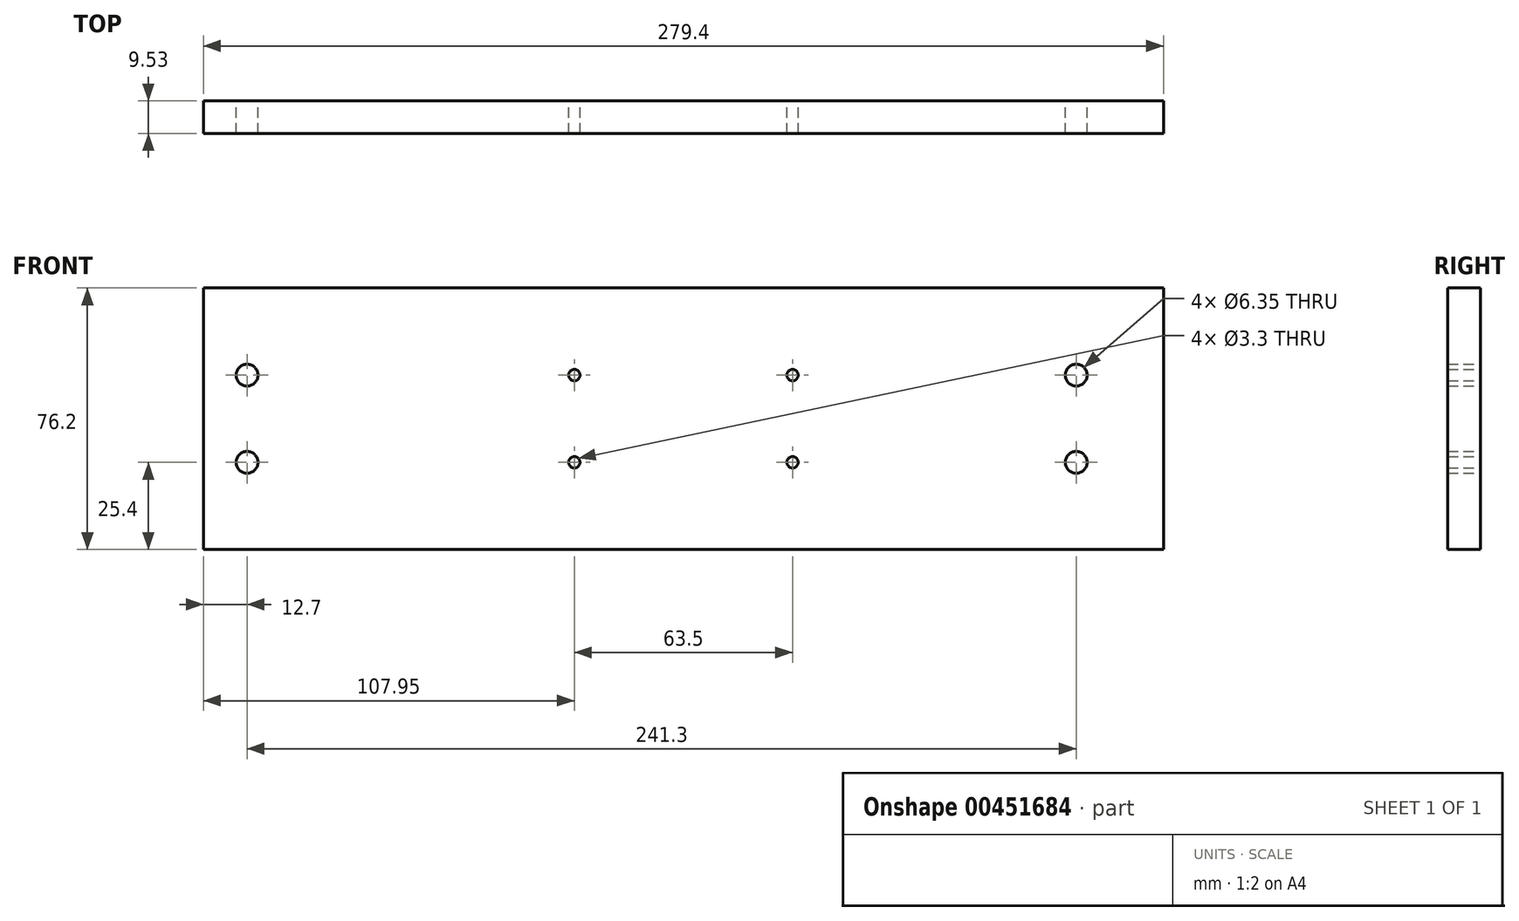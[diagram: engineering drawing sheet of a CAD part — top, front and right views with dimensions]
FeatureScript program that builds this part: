
annotation { "Feature Type Name" : "Feature", "Feature Type Description" : "" }
export const myFeature = defineFeature(function(context is Context, id is Id, definition is map)
    precondition{}
    {
        {
            var Q0;
            Q0=qCreatedBy(makeId("Front.planeOp"),FACE);
            var sketch = newSketch(context, id + "F0", { "sketchPlane" : qUnion([Q0])});
            skLineSegment(sketch, "E0.bottom", {"start": v(-139.7, 38.1) * mm, "end": v(139.7, 38.1) * mm});
            skLineSegment(sketch, "E0.left", {"start": v(-139.7, 38.1) * mm, "end": v(-139.7, 0) * mm});
            skLineSegment(sketch, "E0.right", {"start": v(139.7, 38.1) * mm, "end": v(139.7, 0) * mm});
            skCircle(sketch, "E1", {"center": v(-127, 12.7) * mm, "radius": 3.18 * mm});
            skCircle(sketch, "E2", {"center": v(-31.75, 12.7) * mm, "radius": 1.65 * mm});
            skCircle(sketch, "E3", {"center": v(31.75, 12.7) * mm, "radius": 1.65 * mm});
            skCircle(sketch, "E4", {"center": v(114.3, 12.7) * mm, "radius": 3.18 * mm});
            skCircle(sketch, "E5.MirrorC", {"center": v(114.3, -12.7) * mm, "radius": 3.18 * mm});
            skCircle(sketch, "E6.MirrorC", {"center": v(31.75, -12.7) * mm, "radius": 1.65 * mm});
            skCircle(sketch, "E7.MirrorC", {"center": v(-31.75, -12.7) * mm, "radius": 1.65 * mm});
            skCircle(sketch, "E8.MirrorC", {"center": v(-127, -12.7) * mm, "radius": 3.18 * mm});
            skLineSegment(sketch, "E9.MirrorCS", {"start": v(-139.7, -38.1) * mm, "end": v(139.7, -38.1) * mm});
            skLineSegment(sketch, "E10.MirrorCS", {"start": v(-139.7, -38.1) * mm, "end": v(-139.7, 0) * mm});
            skLineSegment(sketch, "E11.MirrorCS", {"start": v(139.7, -38.1) * mm, "end": v(139.7, 0) * mm});
            skSolve(sketch);
        }
        {
            var Q0;
            Q0 = qSketchRegion(id + "F0", true);
            extrude(context, id + "F1", {"entities" : qUnion([Q0]), "depth" : 9.52 * mm});
        }
    });
